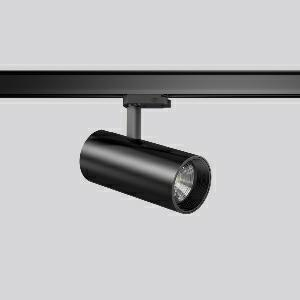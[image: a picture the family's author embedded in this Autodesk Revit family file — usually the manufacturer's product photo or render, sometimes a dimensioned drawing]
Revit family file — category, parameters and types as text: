
# Revit family: deecos_s_mini_742208_003_3_72d6
name_source: partatom
category: Lighting Fixtures
units: mm (PartAtom-declared; Revit-internal decimal feet)

## family parameters
Cut with Voids When Loaded = No
Host = Face
Light Source = No
Part Type = Normal
Room Calculation Point = No
Round Connector Dimension = Use Diameter
Shared = No

## types (1)
- DEECOS S mini (1 x LED Modul 935, 2900 lm, 3500)
    Apparent Load = 29 VA
    Approval mark = CE
    CIE Flux Codes = 98 100 100 100 100
    Color Rendering = 92
    Color Temperature = 3500
    Default Elevation = 1800 mm
    Description = Series: DEECOS S mini
LED surface-mounted projector in modern design with no visible cooling ribs. Housing: die-cast aluminium, powder-coated. Rotation range: 356°. Swivel range: 90°. Black plastic ring and recessed LED to prevent glare from the side. Optical assembly with lens made of plastic (polycarbonate) for the best homogeneous light distribution - can be changed without tools. Best colour rendering index Ra>90. With multi adaptor for 3-circuit tracks 230 V. Suitable for Track on ceiling, Wall track. High quality converter without flickering and stroboscopic effect. The following accessories can be mounted without use of tools: interchangeable lenses, decorative glasses, honeycomb louvre, clear and frosted diffusers, white interchangeable plastic ring. 
Colour: deep black, matt (RAL 9005)
Diameter: 87 mm
Height: 214 mm
Lamp: LED
Socket: without socket
Colour temperature: 3500K
Colour rendering index (CRI): 92
System power: 29 W
Rated luminous flux: 2900 lm
Luminous efficiency: 100 lm/W
Control gear: Regulated power supply
Protection class: I
Type of protection: IP 20
    Height = 214 mm
    Lamp = 1 x LED Modul 935
    Lamp Light Flux = 2900 lm
    Lamp count = 1
    Length = 87 mm
    Lifetime = 50000 h
    Luminous efficacy = 100 lm/W
    Manufacturer = RZB
    ModVariant = No
    Model = 742208.003.3
    Mounting Place = Ceiling
    Mounting Type = Rail mounted
    Number of Poles = 1
    OnlyDefault = Yes
    Power Factor = 1
    Product Name = DEECOS S mini
    Product group = Track mounted projectors
    ProductGroupID = 301
    Protection Class = Protection class I
    Protection Degree = IP 20
    RLX_Detail_Level = 1
    RLX_Emergency_Light_Flux = 0 lm
    RLX_Emergency_Type = 0
    RLX_Emergency_Type_DB = No
    RlxData = <blob elided: 38729 chars, md5=2d07f44e>
    Socket = socket
    Standby Power = 0 W
    System Light Flux = 2900 lm
    System Power = 29 W
    Type Comments = Product without accessories
    Type Image = 741930.003.jpg
    URL = http://relux.com
    VarID = ---
    Voltage = 230 V
    Voltage Range = 220-240 V
    Weight = 0.00 kg
    Width = 0 mm  [stored 0 ft]

note: [stored X ft] marks values corroborated as IEEE doubles in the binary element streams (Revit-internal decimal feet)

## geometry (parser evidence)
native form markers: Blend x4, Sweep x13
no freeform markers — native parametric forms only
